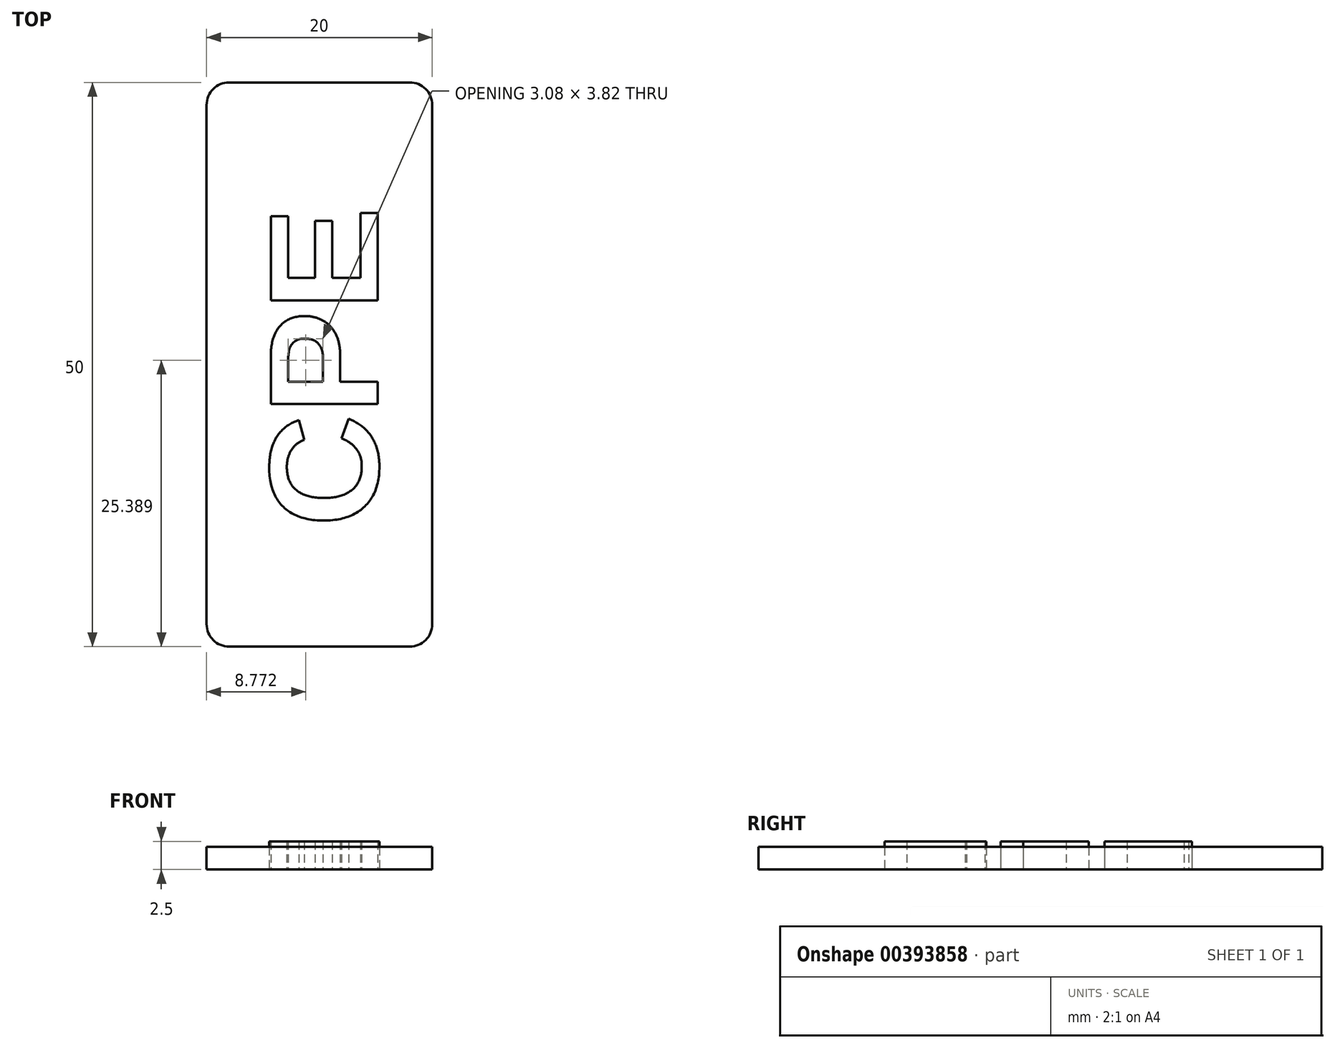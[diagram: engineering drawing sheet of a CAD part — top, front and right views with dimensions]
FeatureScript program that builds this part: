
annotation { "Feature Type Name" : "Feature", "Feature Type Description" : "" }
export const myFeature = defineFeature(function(context is Context, id is Id, definition is map)
    precondition{}
    {
        {
            var Q0;
            Q0=qCreatedBy(makeId("Top.planeOp"),FACE);
            var sketch = newSketch(context, id + "F0", { "sketchPlane" : qUnion([Q0])});
            skLineSegment(sketch, "E0.bottom", {"start": v(-20, -25) * mm, "end": v(0, -25) * mm});
            skLineSegment(sketch, "E0.top", {"start": v(-20, 25) * mm, "end": v(0, 25) * mm});
            skLineSegment(sketch, "E0.left", {"start": v(-20, -25) * mm, "end": v(-20, 25) * mm});
            skLineSegment(sketch, "E0.right", {"start": v(0, -25) * mm, "end": v(0, 25) * mm});
            skSolve(sketch);
        }
        {
            var Q0;
            Q0=makeQuery(id+"F0.imprint","IMPRINT",FACE,{"disambiguationData":[TD([[makeQuery(id+"F0.imprint","IMPRINT",EDGE,{"derivedFrom":sQuery(id+"F0.wireOp",EDGE,"E0.bottom")}),1.0]])]});
            extrude(context, id + "F1", {"entities" : qUnion([Q0]), "depth" : 2 * mm});
        }
        {
            var Q0;
            Q0=makeQuery(id+"F1.opExtrude","SWEPT_EDGE",EDGE,{"disambiguationData":[OSD([sQuery(id+"F0.wireOp",EDGE,"E0.bottom"),sQuery(id+"F0.wireOp",EDGE,"E0.right")])]});
            var Q1;
            Q1=makeQuery(id+"F1.opExtrude","SWEPT_EDGE",EDGE,{"disambiguationData":[OSD([sQuery(id+"F0.wireOp",EDGE,"E0.bottom"),sQuery(id+"F0.wireOp",EDGE,"E0.left")])]});
            var Q2;
            Q2=makeQuery(id+"F1.opExtrude","SWEPT_EDGE",EDGE,{"disambiguationData":[OSD([sQuery(id+"F0.wireOp",EDGE,"E0.top"),sQuery(id+"F0.wireOp",EDGE,"E0.right")])]});
            var Q3;
            Q3=makeQuery(id+"F1.opExtrude","SWEPT_EDGE",EDGE,{"disambiguationData":[OSD([sQuery(id+"F0.wireOp",EDGE,"E0.top"),sQuery(id+"F0.wireOp",EDGE,"E0.left")])]});
            fillet(context, id + "F2", {"entities" : qUnion([Q0, Q1, Q2, Q3]), "radius" : 2 * mm, "tangentPropagation" : true, "allowEdgeOverflow" : false});
        }
        {
            var Q0;
            Q0=qCreatedBy(makeId("Top.planeOp"),FACE);
            var sketch = newSketch(context, id + "F3", { "sketchPlane" : qUnion([Q0])});
            skText(sketch, "E1", { "text": "CPE", "fontName": "Arimo-Bold.ttf"});
            const initialGuessF3  = {"E1": [-0.00482, -0.01439, 0, 1, 0.00993]};
            skSetInitialGuess(sketch, initialGuessF3);
            skSolve(sketch);
        }
        {
            var Q0;
            Q0=qSketchRegion(id+"F3",true);
            extrude(context, id + "F4", {"entities" : qUnion([Q0]), "depth" : 2.5 * mm});
        }
    });
